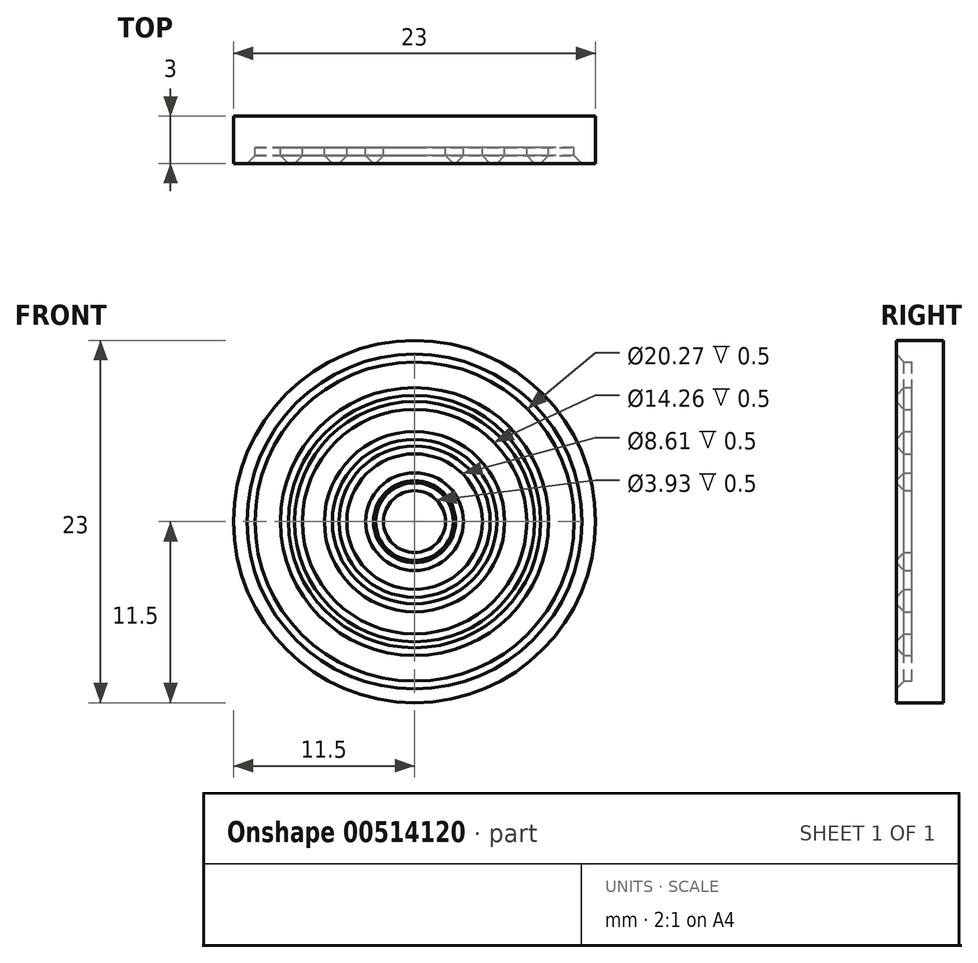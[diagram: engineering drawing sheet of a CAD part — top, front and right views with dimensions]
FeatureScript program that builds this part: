
annotation { "Feature Type Name" : "Feature", "Feature Type Description" : "" }
export const myFeature = defineFeature(function(context is Context, id is Id, definition is map)
    precondition{}
    {
        {
            var Q0;
            Q0=qCreatedBy(makeId("Front.planeOp"),FACE);
            var sketch = newSketch(context, id + "F0", { "sketchPlane" : qUnion([Q0])});
            skCircle(sketch, "E0", {"center": v(0, 0) * mm, "radius": 11.5 * mm});
            skSolve(sketch);
        }
        {
            var Q0;
            Q0=makeQuery(id+"F0.imprint","IMPRINT",FACE,{"disambiguationData":[TD([[makeQuery(id+"F0.imprint","IMPRINT",EDGE,{"derivedFrom":sQuery(id+"F0.wireOp",EDGE,"E0")}),1.0]])]});
            extrude(context, id + "F1", {"entities" : qUnion([Q0]), "depth" : 2 * mm});
        }
        {
            var Q0;
            Q0=makeQuery(id+"F1.opExtrude","CAP_FACE",FACE,{"disambiguationData":[OSD([sQuery(id+"F0.wireOp",EDGE,"E0")])],"isStart":false});
            var sketch = newSketch(context, id + "F2", { "sketchPlane" : qUnion([Q0])});
            skCircle(sketch, "E1", {"center": v(0, 0) * mm, "radius": 11.71 * mm});
            skCircle(sketch, "E2", {"center": v(0, 0) * mm, "radius": 10.13 * mm});
            skCircle(sketch, "E3", {"center": v(0, 0) * mm, "radius": 8.51 * mm});
            skCircle(sketch, "E4", {"center": v(0, 0) * mm, "radius": 7.13 * mm});
            skCircle(sketch, "E5", {"center": v(0, 0) * mm, "radius": 5.72 * mm});
            skCircle(sketch, "E6", {"center": v(0, 0) * mm, "radius": 4.3 * mm});
            skCircle(sketch, "E7", {"center": v(0, 0) * mm, "radius": 3.1 * mm});
            skCircle(sketch, "E8", {"center": v(0, 0) * mm, "radius": 1.96 * mm});
            skSolve(sketch);
        }
        {
            var Q0;
            Q0=makeQuery(id+"F2.imprint","IMPRINT",FACE,{"disambiguationData":[TD([[makeQuery(id+"F2.imprint","IMPRINT",EDGE,{"derivedFrom":sQuery(id+"F2.wireOp",EDGE,"E2")}),-1.0]])]});
            var Q1;
            Q1=makeQuery(id+"F2.imprint","IMPRINT",FACE,{"disambiguationData":[TD([[makeQuery(id+"F2.imprint","IMPRINT",EDGE,{"derivedFrom":sQuery(id+"F2.wireOp",EDGE,"E3")}),1.0]])]});
            var Q2;
            Q2=makeQuery(id+"F2.imprint","IMPRINT",FACE,{"disambiguationData":[TD([[makeQuery(id+"F2.imprint","IMPRINT",EDGE,{"derivedFrom":sQuery(id+"F2.wireOp",EDGE,"E5")}),1.0]])]});
            var Q3;
            Q3=makeQuery(id+"F2.imprint","IMPRINT",FACE,{"disambiguationData":[TD([[makeQuery(id+"F2.imprint","IMPRINT",EDGE,{"derivedFrom":sQuery(id+"F2.wireOp",EDGE,"E7")}),1.0]])]});
            extrude(context, id + "F3", {"entities" : qUnion([Q0, Q1, Q2, Q3]), "operationType" : NewBodyOperationType.ADD, "depth" : 1 * mm, "offsetDistance" : 25 * mm});
        }
        {
            var Q0;
            Q0=makeQuery(id+"F3.opExtrude","CAP_EDGE",EDGE,{"disambiguationData":[OSD([sQuery(id+"F2.wireOp",EDGE,"E8")])],"isStart":false});
            var Q1;
            Q1=makeQuery(id+"F3.opExtrude","CAP_EDGE",EDGE,{"disambiguationData":[OSD([sQuery(id+"F2.wireOp",EDGE,"E6")])],"isStart":false});
            var Q2;
            Q2=makeQuery(id+"F3.opExtrude","CAP_EDGE",EDGE,{"disambiguationData":[OSD([sQuery(id+"F2.wireOp",EDGE,"E4")])],"isStart":false});
            var Q3;
            Q3=makeQuery(id+"F3.opExtrude","CAP_EDGE",EDGE,{"disambiguationData":[OSD([sQuery(id+"F2.wireOp",EDGE,"E2")])],"isStart":false});
            chamfer(context, id + "F4", {"entities" : qUnion([Q0, Q1, Q2, Q3]), "width" : 0.5 * mm, "tangentPropagation" : true});
        }
        {
            var Q0;
            Q0=makeQuery(id+"F3.opExtrude","CAP_EDGE",EDGE,{"disambiguationData":[OSD([sQuery(id+"F2.wireOp",EDGE,"E7")])],"isStart":false});
            var Q1;
            Q1=makeQuery(id+"F3.opExtrude","CAP_EDGE",EDGE,{"disambiguationData":[OSD([sQuery(id+"F2.wireOp",EDGE,"E5")])],"isStart":false});
            var Q2;
            Q2=makeQuery(id+"F3.opExtrude","CAP_EDGE",EDGE,{"disambiguationData":[OSD([sQuery(id+"F2.wireOp",EDGE,"E3")])],"isStart":false});
            chamfer(context, id + "F5", {"entities" : qUnion([Q0, Q1, Q2]), "width" : 0.5 * mm, "tangentPropagation" : true});
        }
    });
